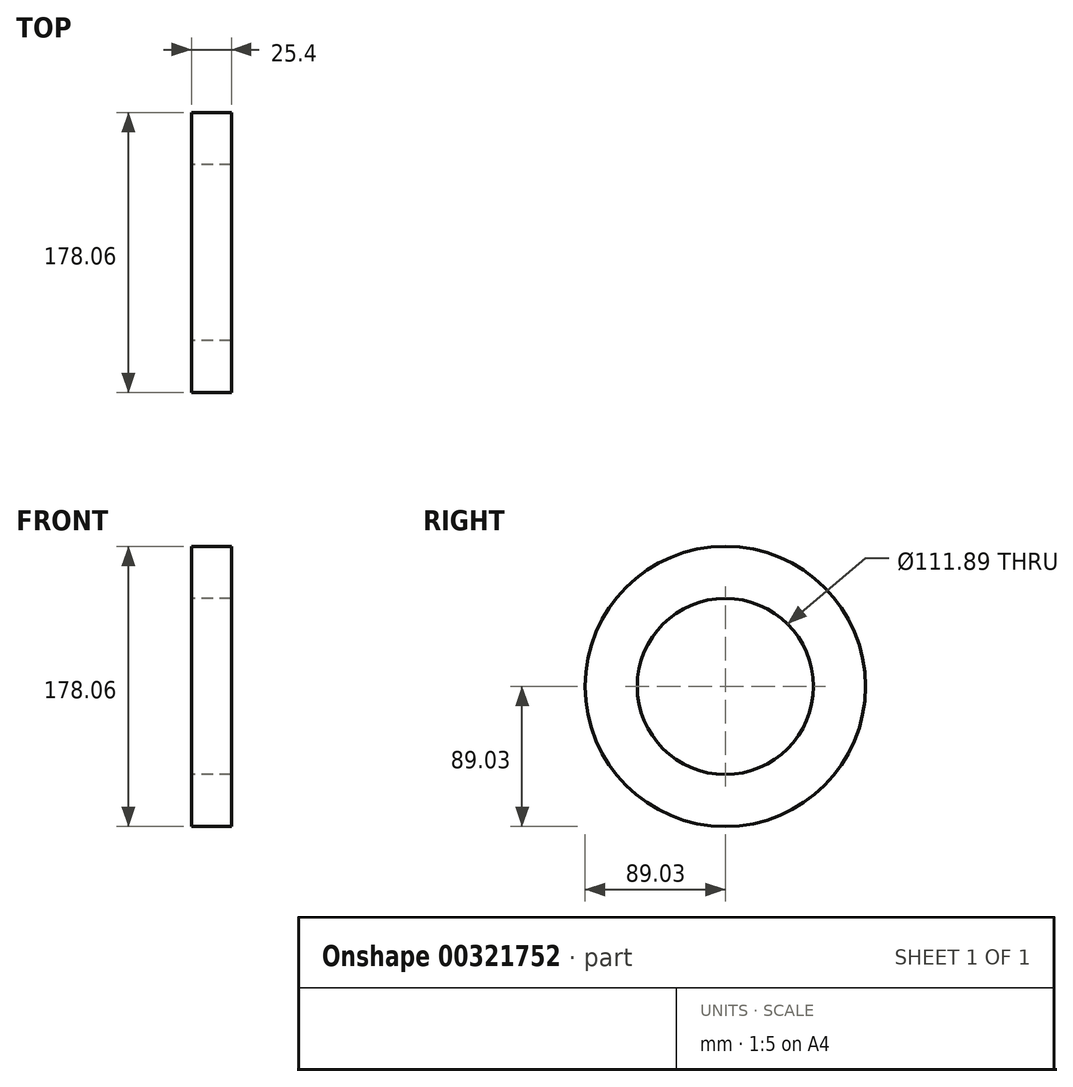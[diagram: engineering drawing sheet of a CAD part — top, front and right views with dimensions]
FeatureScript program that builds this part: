
annotation { "Feature Type Name" : "Feature", "Feature Type Description" : "" }
export const myFeature = defineFeature(function(context is Context, id is Id, definition is map)
    precondition{}
    {
        {
            var Q0;
            Q0=qCreatedBy(makeId("Right.planeOp"),FACE);
            var sketch = newSketch(context, id + "F0", { "sketchPlane" : qUnion([Q0])});
            skCircle(sketch, "E0", {"center": v(0, 0) * mm, "radius": 55.95 * mm});
            skSolve(sketch);
        }
        {
            var Q0;
            Q0=qCreatedBy(makeId("Right.planeOp"),FACE);
            var sketch = newSketch(context, id + "F1", { "sketchPlane" : qUnion([Q0])});
            skCircle(sketch, "E1", {"center": v(0, 0) * mm, "radius": 89.03 * mm});
            skCircle(sketch, "E2", {"center": v(0, 0) * mm, "radius": 55.95 * mm});
            skSolve(sketch);
        }
        {
            var Q0;
            Q0 = qSketchRegion(id + "F1", true);
            extrude(context, id + "F2", {"entities" : qUnion([Q0]), "endBound" : BoundingType.SYMMETRIC, "depth" : 25.4 * mm});
        }
    });
